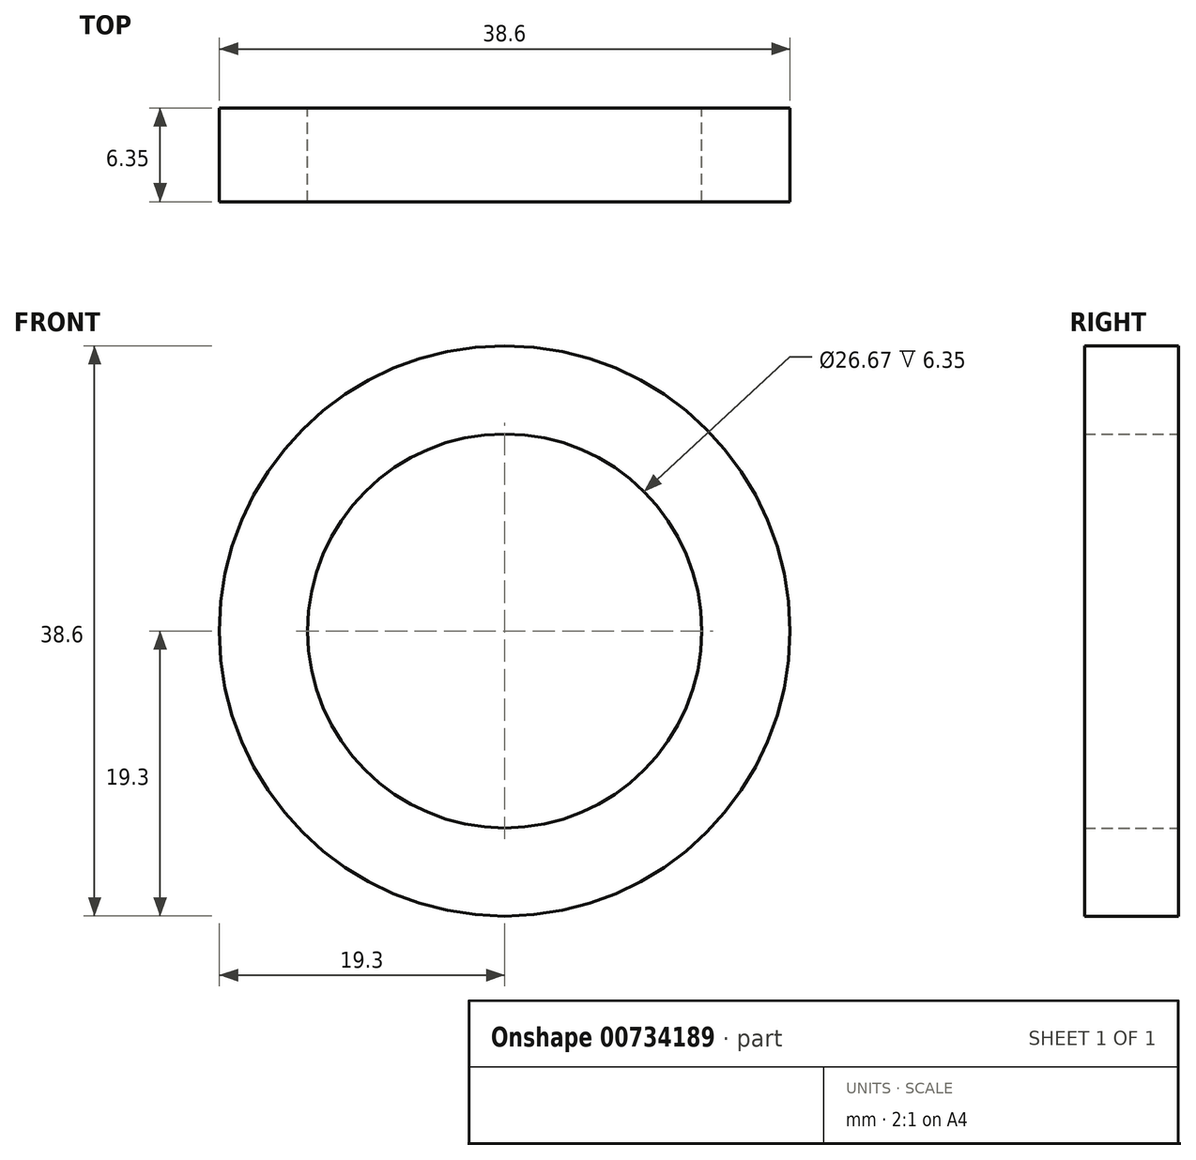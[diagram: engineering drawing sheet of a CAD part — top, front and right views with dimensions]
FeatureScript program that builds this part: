
annotation { "Feature Type Name" : "Feature", "Feature Type Description" : "" }
export const myFeature = defineFeature(function(context is Context, id is Id, definition is map)
    precondition{}
    {
        {
            var Q0;
            Q0=qCreatedBy(makeId("Front.planeOp"),FACE);
            var sketch = newSketch(context, id + "F0", { "sketchPlane" : qUnion([Q0])});
            skCircle(sketch, "E0", {"center": v(0, 0) * mm, "radius": 13.34 * mm});
            skCircle(sketch, "E1", {"center": v(0, 0) * mm, "radius": 19.3 * mm});
            skSolve(sketch);
        }
        {
            var Q0;
            Q0=makeQuery(id+"F0.imprint","IMPRINT",FACE,{"disambiguationData":[TD([[makeQuery(id+"F0.imprint","IMPRINT",EDGE,{"derivedFrom":sQuery(id+"F0.wireOp",EDGE,"E0")}),-1.0]])]});
            extrude(context, id + "F1", {"entities" : qUnion([Q0]), "depth" : 6.35 * mm, "offsetDistance" : 25.4 * mm});
        }
    });
